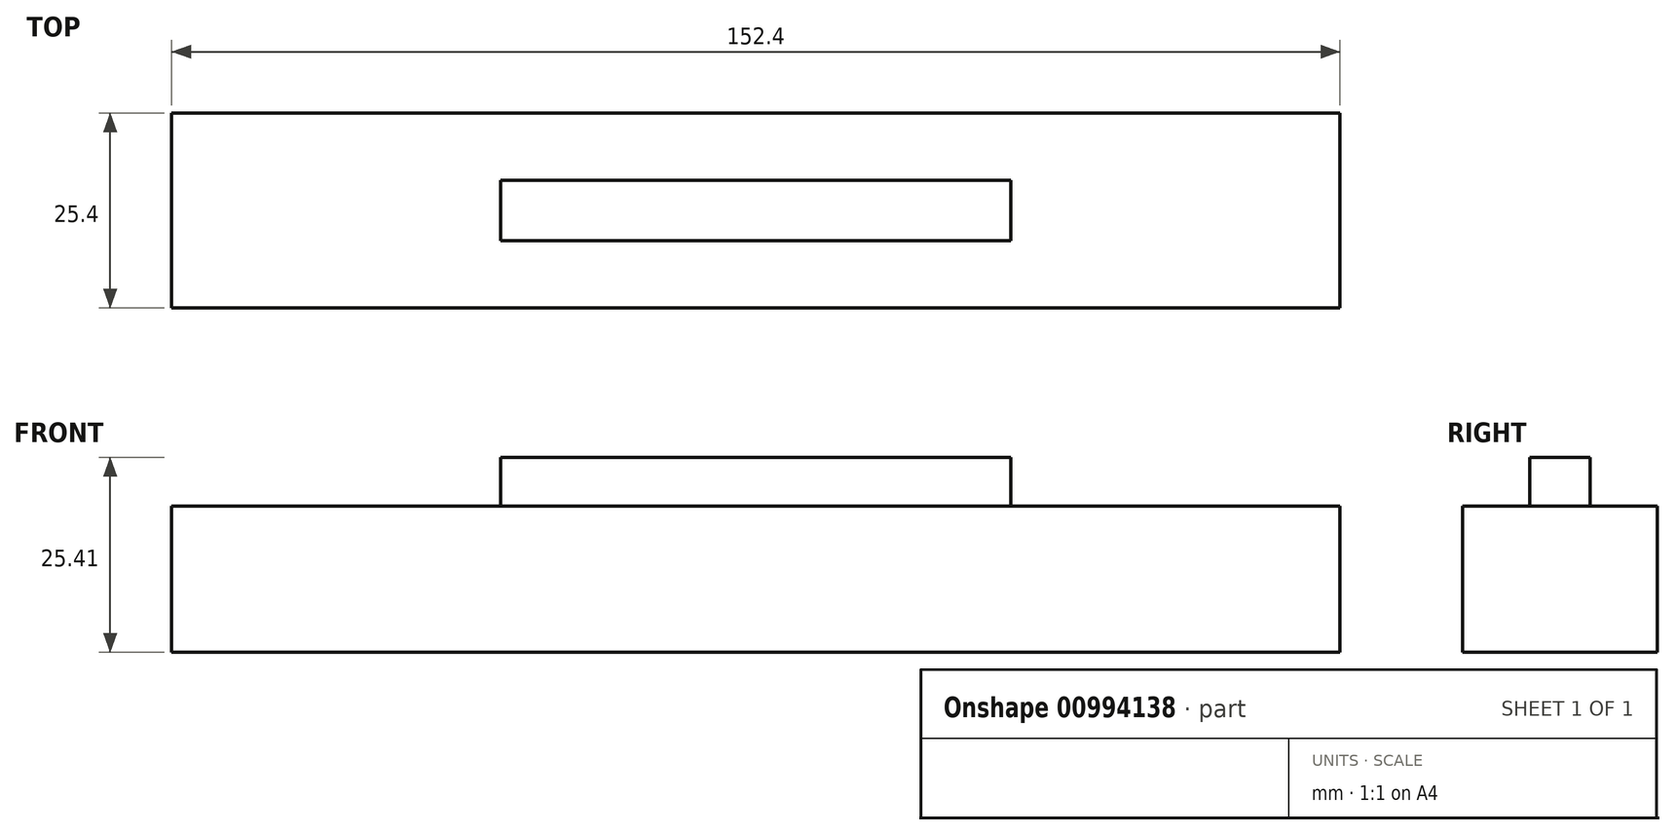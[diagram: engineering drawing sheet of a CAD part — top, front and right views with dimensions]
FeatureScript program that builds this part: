
annotation { "Feature Type Name" : "Feature", "Feature Type Description" : "" }
export const myFeature = defineFeature(function(context is Context, id is Id, definition is map)
    precondition{}
    {
        {
            var Q0;
            Q0=qCreatedBy(makeId("Front.planeOp"),FACE);
            var sketch = newSketch(context, id + "F0", { "sketchPlane" : qUnion([Q0])});
            skLineSegment(sketch, "E0.bottom", {"start": v(-76.2, 9.53) * mm, "end": v(76.2, 9.53) * mm});
            skLineSegment(sketch, "E0.top", {"start": v(-76.2, -9.53) * mm, "end": v(76.2, -9.53) * mm});
            skLineSegment(sketch, "E0.left", {"start": v(-76.2, 9.53) * mm, "end": v(-76.2, -9.53) * mm});
            skLineSegment(sketch, "E0.right", {"start": v(76.2, 9.53) * mm, "end": v(76.2, -9.53) * mm});
            skPoint(sketch, "E0.middle", {"position": v(0, 0) * mm});
            skSolve(sketch);
        }
        {
            var Q0;
            Q0=makeQuery(id+"F0.imprint","IMPRINT",FACE,{"disambiguationData":[TD([[makeQuery(id+"F0.imprint","IMPRINT",EDGE,{"derivedFrom":sQuery(id+"F0.wireOp",EDGE,"E0.bottom")}),-1.0]])]});
            extrude(context, id + "F1", {"entities" : qUnion([Q0]), "depth" : 25.4 * mm, "offsetDistance" : 25.4 * mm});
        }
        {
            var Q0;
            Q0=makeQuery(id+"F1.opExtrude","SWEPT_FACE",FACE,{"disambiguationData":[OSD([sQuery(id+"F0.wireOp",EDGE,"E0.bottom")])]});
            var sketch = newSketch(context, id + "F2", { "sketchPlane" : qUnion([Q0])});
            skLineSegment(sketch, "E1.bottom", {"start": v(-33.28, -8.76) * mm, "end": v(33.28, -8.76) * mm});
            skLineSegment(sketch, "E1.top", {"start": v(-33.28, -16.64) * mm, "end": v(33.28, -16.64) * mm});
            skLineSegment(sketch, "E1.left", {"start": v(-33.28, -8.76) * mm, "end": v(-33.28, -16.64) * mm});
            skLineSegment(sketch, "E1.right", {"start": v(33.28, -8.76) * mm, "end": v(33.28, -16.64) * mm});
            skPoint(sketch, "E1.middle", {"position": v(0, -12.7) * mm});
            skPoint(sketch, "E1.middle.positionSnap0", {"position": v(-76.2, -12.7) * mm});
            skPoint(sketch, "E1.centerSnap0", {"position": v(-76.2, -12.7) * mm});
            skSolve(sketch);
        }
        {
            var Q0;
            Q0 = qSketchRegion(id + "F2", true);
            extrude(context, id + "F3", {"entities" : qUnion([Q0]), "operationType" : NewBodyOperationType.ADD, "depth" : 6.35 * mm, "offsetDistance" : 25.4 * mm});
        }
    });
